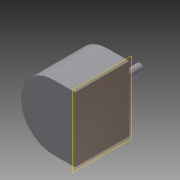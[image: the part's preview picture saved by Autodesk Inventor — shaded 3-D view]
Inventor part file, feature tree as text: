
AUTODESK INVENTOR PART (.ipt)
format: ipt  version: 2014 (Build 180170000, 170)  size: 78,336 bytes
history: native  units: in
note: dims shown in document units (in); Inventor stores cm internally (conversion verified against a paired STEP export)
features: other x3, sketch x2, plane x1
ambient origin geometry x8: Origin, YZ Plane, XZ Plane, XY Plane, X Axis, Y Axis, Z Axis, Center Point
bodies: Solid1 (feature_tree)
feature tree (6):
  other  "motor.ipt"
  other  "Solid1::motor.ipt"
  other  "TaggingFeature1"
  sketch  "Sketch1"  dims[d0=0.3937in]
  sketch  "Sketch2"  dims[d1=1.9685in d2=0.0in d3=0.2756in d4=0.7874in d5=0.0in]
  plane  "Work Plane1"
